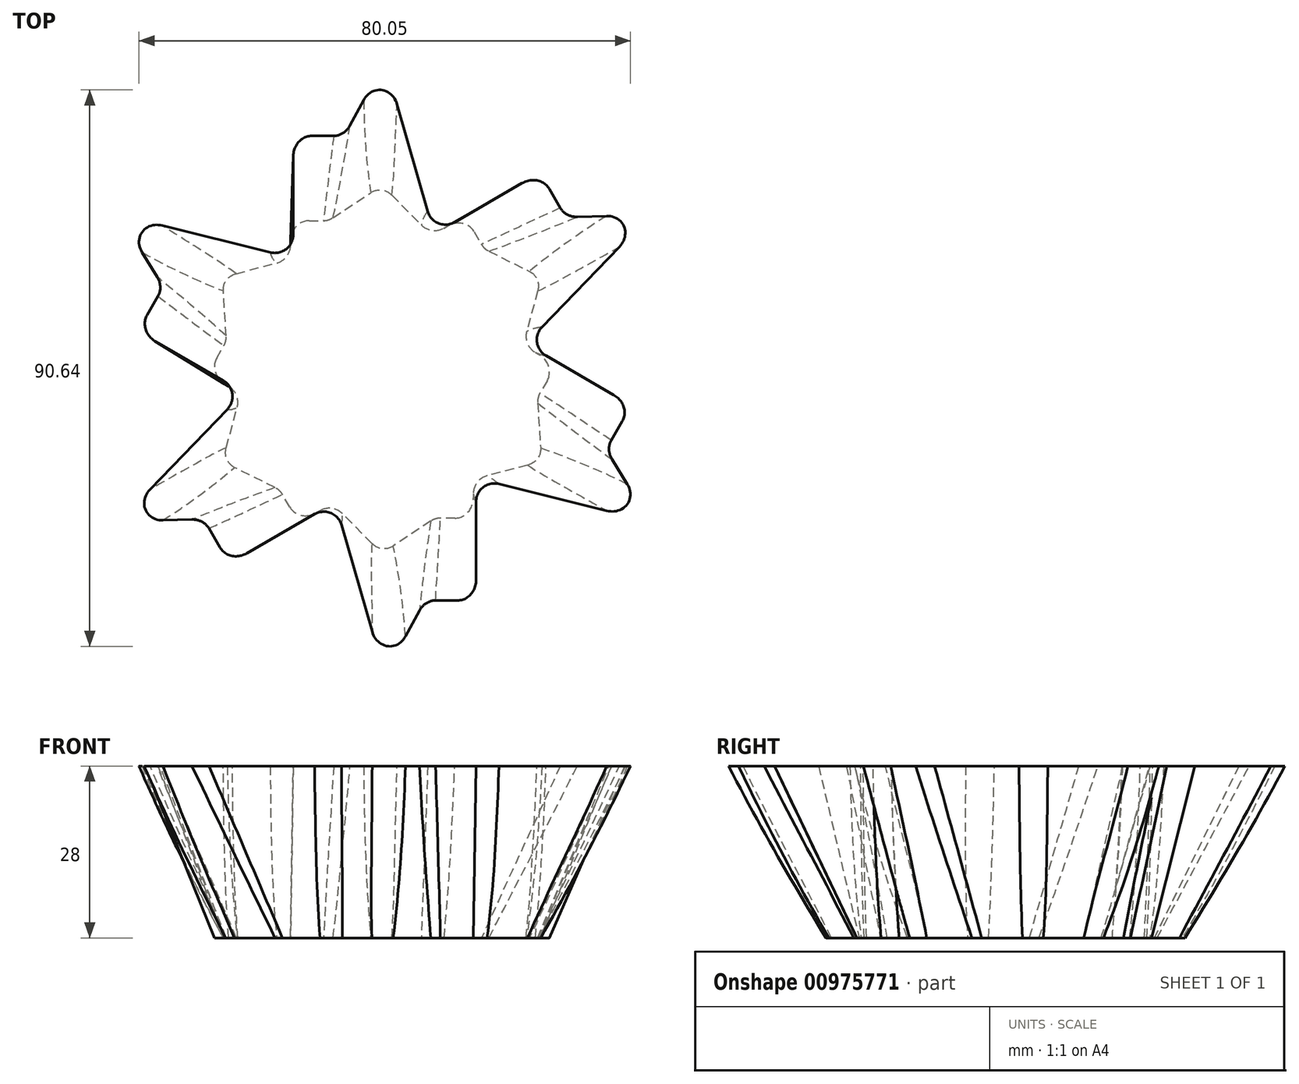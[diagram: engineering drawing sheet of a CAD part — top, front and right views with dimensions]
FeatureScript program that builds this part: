
annotation { "Feature Type Name" : "Feature", "Feature Type Description" : "" }
export const myFeature = defineFeature(function(context is Context, id is Id, definition is map)
    precondition{}
    {
        {
            var Q0;
            Q0=qCreatedBy(makeId("Top.planeOp"),FACE);
            cPlane(context, id + "F0", {"entities" : qUnion([Q0]), "cplaneType" : CPlaneType.OFFSET, "offset" : 28 * mm, "width" : 150 * mm, "height" : 150 * mm});
        }
        {
            var Q0;
            Q0=qCreatedBy(id+"F0.planeOp",FACE);
            cPlane(context, id + "F1", {"entities" : qUnion([Q0]), "cplaneType" : CPlaneType.OFFSET, "offset" : 75 * mm, "width" : 150 * mm, "height" : 150 * mm});
        }
        {
            var Q0;
            Q0=qCreatedBy(makeId("Top.planeOp"),FACE);
            var sketch = newSketch(context, id + "F2", { "sketchPlane" : qUnion([Q0])});
            skLineSegment(sketch, "E0", {"start": v(0, 0) * mm, "end": v(0, 30) * mm});
            skLineSegment(sketch, "E1", {"start": v(0, 30) * mm, "end": v(0, 0) * mm, "construction": true});
            skLineSegment(sketch, "E2", {"start": v(0, 0) * mm, "end": v(-25.98, 15) * mm, "construction": true});
            skLineSegment(sketch, "E3", {"start": v(-25.98, 15) * mm, "end": v(-14.9, 17.92) * mm});
            skLineSegment(sketch, "E4", {"start": v(-14.9, 17.92) * mm, "end": v(-14.9, 24.23) * mm});
            skLineSegment(sketch, "E5", {"start": v(-14.9, 24.23) * mm, "end": v(-8.69, 24.23) * mm});
            skLineSegment(sketch, "E6", {"start": v(-8.69, 24.23) * mm, "end": v(0, 30) * mm});
            skLineSegment(sketch, "E7.1.0", {"start": v(-25.98, -15) * mm, "end": v(-22.97, -3.93) * mm});
            skLineSegment(sketch, "E7.1.1", {"start": v(-22.97, -3.93) * mm, "end": v(-28.43, -0.78) * mm});
            skLineSegment(sketch, "E7.1.2", {"start": v(-28.43, -0.78) * mm, "end": v(-25.33, 4.59) * mm});
            skLineSegment(sketch, "E7.1.3", {"start": v(-25.33, 4.59) * mm, "end": v(-25.98, 15) * mm});
            skLineSegment(sketch, "E7.2.0", {"start": v(0, -30) * mm, "end": v(-8.08, -21.86) * mm});
            skLineSegment(sketch, "E7.2.1", {"start": v(-8.08, -21.86) * mm, "end": v(-13.54, -25) * mm});
            skLineSegment(sketch, "E7.2.2", {"start": v(-13.54, -25) * mm, "end": v(-16.64, -19.64) * mm});
            skLineSegment(sketch, "E7.2.3", {"start": v(-16.64, -19.64) * mm, "end": v(-25.98, -15) * mm});
            skPoint(sketch, "E7.center", {"position": v(0, 0) * mm});
            skLineSegment(sketch, "E8.1.3.0", {"start": v(25.98, -15) * mm, "end": v(14.9, -17.92) * mm});
            skLineSegment(sketch, "E8.3.3.0", {"start": v(14.9, -17.92) * mm, "end": v(14.9, -24.23) * mm});
            skLineSegment(sketch, "E8.6.3.0", {"start": v(14.9, -24.23) * mm, "end": v(8.69, -24.23) * mm});
            skLineSegment(sketch, "E8.9.3.0", {"start": v(8.69, -24.23) * mm, "end": v(0, -30) * mm});
            skLineSegment(sketch, "E8.1.4.0", {"start": v(25.98, 15) * mm, "end": v(22.97, 3.93) * mm});
            skLineSegment(sketch, "E8.3.4.0", {"start": v(22.97, 3.93) * mm, "end": v(28.43, 0.78) * mm});
            skLineSegment(sketch, "E8.6.4.0", {"start": v(28.43, 0.78) * mm, "end": v(25.33, -4.59) * mm});
            skLineSegment(sketch, "E8.9.4.0", {"start": v(25.33, -4.59) * mm, "end": v(25.98, -15) * mm});
            skLineSegment(sketch, "E8.1.5.0", {"start": v(0, 30) * mm, "end": v(8.08, 21.86) * mm});
            skLineSegment(sketch, "E8.3.5.0", {"start": v(8.08, 21.86) * mm, "end": v(13.54, 25) * mm});
            skLineSegment(sketch, "E8.6.5.0", {"start": v(13.54, 25) * mm, "end": v(16.64, 19.64) * mm});
            skLineSegment(sketch, "E8.9.5.0", {"start": v(16.64, 19.64) * mm, "end": v(25.98, 15) * mm});
            skSolve(sketch);
        }
        {
            var Q0;
            Q0=qCreatedBy(id+"F0.planeOp",FACE);
            var sketch = newSketch(context, id + "F3", { "sketchPlane" : qUnion([Q0])});
            skLineSegment(sketch, "E9", {"start": v(0.44, 0.2) * mm, "end": v(0.44, 50.2) * mm});
            skLineSegment(sketch, "E10", {"start": v(0.44, 50.2) * mm, "end": v(0.44, 0.2) * mm, "construction": true});
            skLineSegment(sketch, "E11", {"start": v(0.44, 0.2) * mm, "end": v(-42.86, 25.2) * mm, "construction": true});
            skLineSegment(sketch, "E12", {"start": v(-42.86, 25.2) * mm, "end": v(-14.45, 18.12) * mm});
            skLineSegment(sketch, "E13", {"start": v(-14.45, 18.12) * mm, "end": v(-14.45, 38.04) * mm});
            skLineSegment(sketch, "E14", {"start": v(-14.45, 38.04) * mm, "end": v(-6.12, 38.04) * mm});
            skLineSegment(sketch, "E15", {"start": v(-6.12, 38.04) * mm, "end": v(0.44, 50.2) * mm});
            skLineSegment(sketch, "E16.1.0", {"start": v(-42.86, -24.8) * mm, "end": v(-22.53, -3.73) * mm});
            skLineSegment(sketch, "E16.1.1", {"start": v(-22.53, -3.73) * mm, "end": v(-39.77, 6.22) * mm});
            skLineSegment(sketch, "E16.1.2", {"start": v(-39.77, 6.22) * mm, "end": v(-35.6, 13.44) * mm});
            skLineSegment(sketch, "E16.1.3", {"start": v(-35.6, 13.44) * mm, "end": v(-42.86, 25.2) * mm});
            skLineSegment(sketch, "E16.2.0", {"start": v(0.44, -49.8) * mm, "end": v(-7.64, -21.66) * mm});
            skLineSegment(sketch, "E16.2.1", {"start": v(-7.64, -21.66) * mm, "end": v(-24.88, -31.61) * mm});
            skLineSegment(sketch, "E16.2.2", {"start": v(-24.88, -31.61) * mm, "end": v(-29.05, -24.4) * mm});
            skLineSegment(sketch, "E16.2.3", {"start": v(-29.05, -24.4) * mm, "end": v(-42.86, -24.8) * mm});
            skPoint(sketch, "E16.center", {"position": v(0.44, 0.2) * mm});
            skLineSegment(sketch, "E17.1.3.0", {"start": v(43.74, -24.8) * mm, "end": v(15.33, -17.72) * mm});
            skLineSegment(sketch, "E17.3.3.0", {"start": v(15.33, -17.72) * mm, "end": v(15.33, -37.64) * mm});
            skLineSegment(sketch, "E17.6.3.0", {"start": v(15.33, -37.64) * mm, "end": v(7, -37.64) * mm});
            skLineSegment(sketch, "E17.9.3.0", {"start": v(7, -37.64) * mm, "end": v(0.44, -49.8) * mm});
            skLineSegment(sketch, "E17.1.4.0", {"start": v(43.74, 25.2) * mm, "end": v(23.4, 4.13) * mm});
            skLineSegment(sketch, "E17.3.4.0", {"start": v(23.4, 4.13) * mm, "end": v(40.65, -5.82) * mm});
            skLineSegment(sketch, "E17.6.4.0", {"start": v(40.65, -5.82) * mm, "end": v(36.49, -13.04) * mm});
            skLineSegment(sketch, "E17.9.4.0", {"start": v(36.49, -13.04) * mm, "end": v(43.74, -24.8) * mm});
            skLineSegment(sketch, "E17.1.5.0", {"start": v(0.44, 50.2) * mm, "end": v(8.52, 22.06) * mm});
            skLineSegment(sketch, "E17.3.5.0", {"start": v(8.52, 22.06) * mm, "end": v(25.76, 32.01) * mm});
            skLineSegment(sketch, "E17.6.5.0", {"start": v(25.76, 32.01) * mm, "end": v(29.93, 24.8) * mm});
            skLineSegment(sketch, "E17.9.5.0", {"start": v(29.93, 24.8) * mm, "end": v(43.74, 25.2) * mm});
            skSolve(sketch);
        }
        {
            var Q0;
            Q0=qCreatedBy(id+"F1.planeOp",FACE);
            cPlane(context, id + "F4", {"entities" : qUnion([Q0]), "cplaneType" : CPlaneType.OFFSET, "offset" : 25 * mm, "width" : 150 * mm, "height" : 150 * mm});
        }
        {
            var Q0;
            Q0=makeQuery(id+"F3.imprint","IMPRINT",FACE,{"disambiguationData":[TD([[makeQuery(id+"F3.imprint","IMPRINT",EDGE,{"derivedFrom":sQuery(id+"F3.wireOp",EDGE,"E12")}),-1.0]])]});
            var Q1;
            Q1=makeQuery(id+"F2.imprint","IMPRINT",FACE,{"disambiguationData":[TD([[makeQuery(id+"F2.imprint","IMPRINT",EDGE,{"derivedFrom":sQuery(id+"F2.wireOp",EDGE,"E3")}),-1.0]])]});
            var Q2;
            Q2=makeQuery(id+"F3.imprint","IMPRINT",FACE,{"disambiguationData":[TD([[makeQuery(id+"F3.imprint","IMPRINT",EDGE,{"derivedFrom":sQuery(id+"F3.wireOp",EDGE,"E12")}),-1.0]])]});
            var Q3;
            Q3=makeQuery(id+"F2.imprint","IMPRINT",FACE,{"disambiguationData":[TD([[makeQuery(id+"F2.imprint","IMPRINT",EDGE,{"derivedFrom":sQuery(id+"F2.wireOp",EDGE,"E3")}),-1.0]])]});
            loft(context, id + "F5", {"sheetProfilesArray" : [{ "sheetProfileEntities" : qUnion([Q0]) }, { "sheetProfileEntities" : qUnion([Q1]) }], "wireProfilesArray" : [{ "wireProfileEntities" : qUnion([Q2]) }, { "wireProfileEntities" : qUnion([Q3]) }]});
        }
        {
            var Q0;
            Q0=makeQuery(id+"F5.opLoft","SWEPT_EDGE",EDGE,{"disambiguationData":[OSD([sQuery(id+"F2.wireOp",EDGE,"E7.2.1"),sQuery(id+"F2.wireOp",EDGE,"E7.2.2"),sQuery(id+"F3.wireOp",EDGE,"E16.2.1"),sQuery(id+"F3.wireOp",EDGE,"E16.2.2")])]});
            var Q1;
            Q1=makeQuery(id+"F5.opLoft","SWEPT_EDGE",EDGE,{"disambiguationData":[OSD([sQuery(id+"F2.wireOp",EDGE,"E7.2.2"),sQuery(id+"F2.wireOp",EDGE,"E7.2.3"),sQuery(id+"F3.wireOp",EDGE,"E16.2.2"),sQuery(id+"F3.wireOp",EDGE,"E16.2.3")])]});
            var Q2;
            Q2=makeQuery(id+"F5.opLoft","SWEPT_EDGE",EDGE,{"disambiguationData":[OSD([sQuery(id+"F2.wireOp",EDGE,"E7.1.0"),sQuery(id+"F2.wireOp",EDGE,"E7.2.3"),sQuery(id+"F3.wireOp",EDGE,"E16.1.0"),sQuery(id+"F3.wireOp",EDGE,"E16.2.3")])]});
            var Q3;
            Q3=makeQuery(id+"F5.opLoft","SWEPT_EDGE",EDGE,{"disambiguationData":[OSD([sQuery(id+"F2.wireOp",EDGE,"E7.1.0"),sQuery(id+"F2.wireOp",EDGE,"E7.1.1"),sQuery(id+"F3.wireOp",EDGE,"E16.1.0"),sQuery(id+"F3.wireOp",EDGE,"E16.1.1")])]});
            var Q4;
            Q4=makeQuery(id+"F5.opLoft","SWEPT_EDGE",EDGE,{"disambiguationData":[OSD([sQuery(id+"F2.wireOp",EDGE,"E7.1.1"),sQuery(id+"F2.wireOp",EDGE,"E7.1.2"),sQuery(id+"F3.wireOp",EDGE,"E16.1.1"),sQuery(id+"F3.wireOp",EDGE,"E16.1.2")])]});
            var Q5;
            Q5=makeQuery(id+"F5.opLoft","SWEPT_EDGE",EDGE,{"disambiguationData":[OSD([sQuery(id+"F2.wireOp",EDGE,"E7.1.2"),sQuery(id+"F2.wireOp",EDGE,"E7.1.3"),sQuery(id+"F3.wireOp",EDGE,"E16.1.2"),sQuery(id+"F3.wireOp",EDGE,"E16.1.3")])]});
            var Q6;
            Q6=makeQuery(id+"F5.opLoft","SWEPT_EDGE",EDGE,{"disambiguationData":[OSD([sQuery(id+"F2.wireOp",EDGE,"E3"),sQuery(id+"F2.wireOp",EDGE,"E7.1.3"),sQuery(id+"F3.wireOp",EDGE,"E12"),sQuery(id+"F3.wireOp",EDGE,"E16.1.3")])]});
            var Q7;
            Q7=makeQuery(id+"F5.opLoft","SWEPT_EDGE",EDGE,{"disambiguationData":[OSD([sQuery(id+"F2.wireOp",EDGE,"E3"),sQuery(id+"F2.wireOp",EDGE,"E4"),sQuery(id+"F3.wireOp",EDGE,"E12"),sQuery(id+"F3.wireOp",EDGE,"E13")])]});
            var Q8;
            Q8=makeQuery(id+"F5.opLoft","SWEPT_EDGE",EDGE,{"disambiguationData":[OSD([sQuery(id+"F2.wireOp",EDGE,"E4"),sQuery(id+"F2.wireOp",EDGE,"E5"),sQuery(id+"F3.wireOp",EDGE,"E13"),sQuery(id+"F3.wireOp",EDGE,"E14")])]});
            var Q9;
            Q9=makeQuery(id+"F5.opLoft","SWEPT_EDGE",EDGE,{"disambiguationData":[OSD([sQuery(id+"F2.wireOp",EDGE,"E5"),sQuery(id+"F2.wireOp",EDGE,"E6"),sQuery(id+"F3.wireOp",EDGE,"E14"),sQuery(id+"F3.wireOp",EDGE,"E15")])]});
            var Q10;
            Q10=makeQuery(id+"F5.opLoft","SWEPT_EDGE",EDGE,{"disambiguationData":[OSD([sQuery(id+"F2.wireOp",EDGE,"E6"),sQuery(id+"F2.wireOp",EDGE,"E8.1.5.0"),sQuery(id+"F3.wireOp",EDGE,"E15"),sQuery(id+"F3.wireOp",EDGE,"E17.1.5.0")])]});
            var Q11;
            Q11=makeQuery(id+"F5.opLoft","SWEPT_EDGE",EDGE,{"disambiguationData":[OSD([sQuery(id+"F2.wireOp",EDGE,"E8.1.5.0"),sQuery(id+"F2.wireOp",EDGE,"E8.3.5.0"),sQuery(id+"F3.wireOp",EDGE,"E17.1.5.0"),sQuery(id+"F3.wireOp",EDGE,"E17.3.5.0")])]});
            var Q12;
            Q12=makeQuery(id+"F5.opLoft","SWEPT_EDGE",EDGE,{"disambiguationData":[OSD([sQuery(id+"F2.wireOp",EDGE,"E8.3.5.0"),sQuery(id+"F2.wireOp",EDGE,"E8.6.5.0"),sQuery(id+"F3.wireOp",EDGE,"E17.3.5.0"),sQuery(id+"F3.wireOp",EDGE,"E17.6.5.0")])]});
            var Q13;
            Q13=makeQuery(id+"F5.opLoft","SWEPT_EDGE",EDGE,{"disambiguationData":[OSD([sQuery(id+"F2.wireOp",EDGE,"E8.6.5.0"),sQuery(id+"F2.wireOp",EDGE,"E8.9.5.0"),sQuery(id+"F3.wireOp",EDGE,"E17.6.5.0"),sQuery(id+"F3.wireOp",EDGE,"E17.9.5.0")])]});
            var Q14;
            Q14=makeQuery(id+"F5.opLoft","SWEPT_EDGE",EDGE,{"disambiguationData":[OSD([sQuery(id+"F2.wireOp",EDGE,"E8.1.4.0"),sQuery(id+"F2.wireOp",EDGE,"E8.9.5.0"),sQuery(id+"F3.wireOp",EDGE,"E17.1.4.0"),sQuery(id+"F3.wireOp",EDGE,"E17.9.5.0")])]});
            var Q15;
            Q15=makeQuery(id+"F5.opLoft","SWEPT_EDGE",EDGE,{"disambiguationData":[OSD([sQuery(id+"F2.wireOp",EDGE,"E8.1.4.0"),sQuery(id+"F2.wireOp",EDGE,"E8.3.4.0"),sQuery(id+"F3.wireOp",EDGE,"E17.1.4.0"),sQuery(id+"F3.wireOp",EDGE,"E17.3.4.0")])]});
            var Q16;
            Q16=makeQuery(id+"F5.opLoft","SWEPT_EDGE",EDGE,{"disambiguationData":[OSD([sQuery(id+"F2.wireOp",EDGE,"E8.3.4.0"),sQuery(id+"F2.wireOp",EDGE,"E8.6.4.0"),sQuery(id+"F3.wireOp",EDGE,"E17.3.4.0"),sQuery(id+"F3.wireOp",EDGE,"E17.6.4.0")])]});
            var Q17;
            Q17=makeQuery(id+"F5.opLoft","SWEPT_EDGE",EDGE,{"disambiguationData":[OSD([sQuery(id+"F2.wireOp",EDGE,"E8.6.4.0"),sQuery(id+"F2.wireOp",EDGE,"E8.9.4.0"),sQuery(id+"F3.wireOp",EDGE,"E17.6.4.0"),sQuery(id+"F3.wireOp",EDGE,"E17.9.4.0")])]});
            var Q18;
            Q18=makeQuery(id+"F5.opLoft","SWEPT_EDGE",EDGE,{"disambiguationData":[OSD([sQuery(id+"F2.wireOp",EDGE,"E8.1.3.0"),sQuery(id+"F2.wireOp",EDGE,"E8.9.4.0"),sQuery(id+"F3.wireOp",EDGE,"E17.1.3.0"),sQuery(id+"F3.wireOp",EDGE,"E17.9.4.0")])]});
            var Q19;
            Q19=makeQuery(id+"F5.opLoft","SWEPT_EDGE",EDGE,{"disambiguationData":[OSD([sQuery(id+"F2.wireOp",EDGE,"E8.1.3.0"),sQuery(id+"F2.wireOp",EDGE,"E8.3.3.0"),sQuery(id+"F3.wireOp",EDGE,"E17.1.3.0"),sQuery(id+"F3.wireOp",EDGE,"E17.3.3.0")])]});
            var Q20;
            Q20=makeQuery(id+"F5.opLoft","SWEPT_EDGE",EDGE,{"disambiguationData":[OSD([sQuery(id+"F2.wireOp",EDGE,"E8.3.3.0"),sQuery(id+"F2.wireOp",EDGE,"E8.6.3.0"),sQuery(id+"F3.wireOp",EDGE,"E17.3.3.0"),sQuery(id+"F3.wireOp",EDGE,"E17.6.3.0")])]});
            var Q21;
            Q21=makeQuery(id+"F5.opLoft","SWEPT_EDGE",EDGE,{"disambiguationData":[OSD([sQuery(id+"F2.wireOp",EDGE,"E8.6.3.0"),sQuery(id+"F2.wireOp",EDGE,"E8.9.3.0"),sQuery(id+"F3.wireOp",EDGE,"E17.6.3.0"),sQuery(id+"F3.wireOp",EDGE,"E17.9.3.0")])]});
            var Q22;
            Q22=makeQuery(id+"F5.opLoft","SWEPT_EDGE",EDGE,{"disambiguationData":[OSD([sQuery(id+"F2.wireOp",EDGE,"E7.2.0"),sQuery(id+"F2.wireOp",EDGE,"E8.9.3.0"),sQuery(id+"F3.wireOp",EDGE,"E16.2.0"),sQuery(id+"F3.wireOp",EDGE,"E17.9.3.0")])]});
            var Q23;
            Q23=makeQuery(id+"F5.opLoft","SWEPT_EDGE",EDGE,{"disambiguationData":[OSD([sQuery(id+"F2.wireOp",EDGE,"E7.2.0"),sQuery(id+"F2.wireOp",EDGE,"E7.2.1"),sQuery(id+"F3.wireOp",EDGE,"E16.2.0"),sQuery(id+"F3.wireOp",EDGE,"E16.2.1")])]});
            fillet(context, id + "F6", {"entities" : qUnion([Q0, Q1, Q2, Q3, Q4, Q5, Q6, Q7, Q8, Q9, Q10, Q11, Q12, Q13, Q14, Q15, Q16, Q17, Q18, Q19, Q20, Q21, Q22, Q23]), "radius" : 3 * mm, "tangentPropagation" : true, "allowEdgeOverflow" : false});
        }
    });
